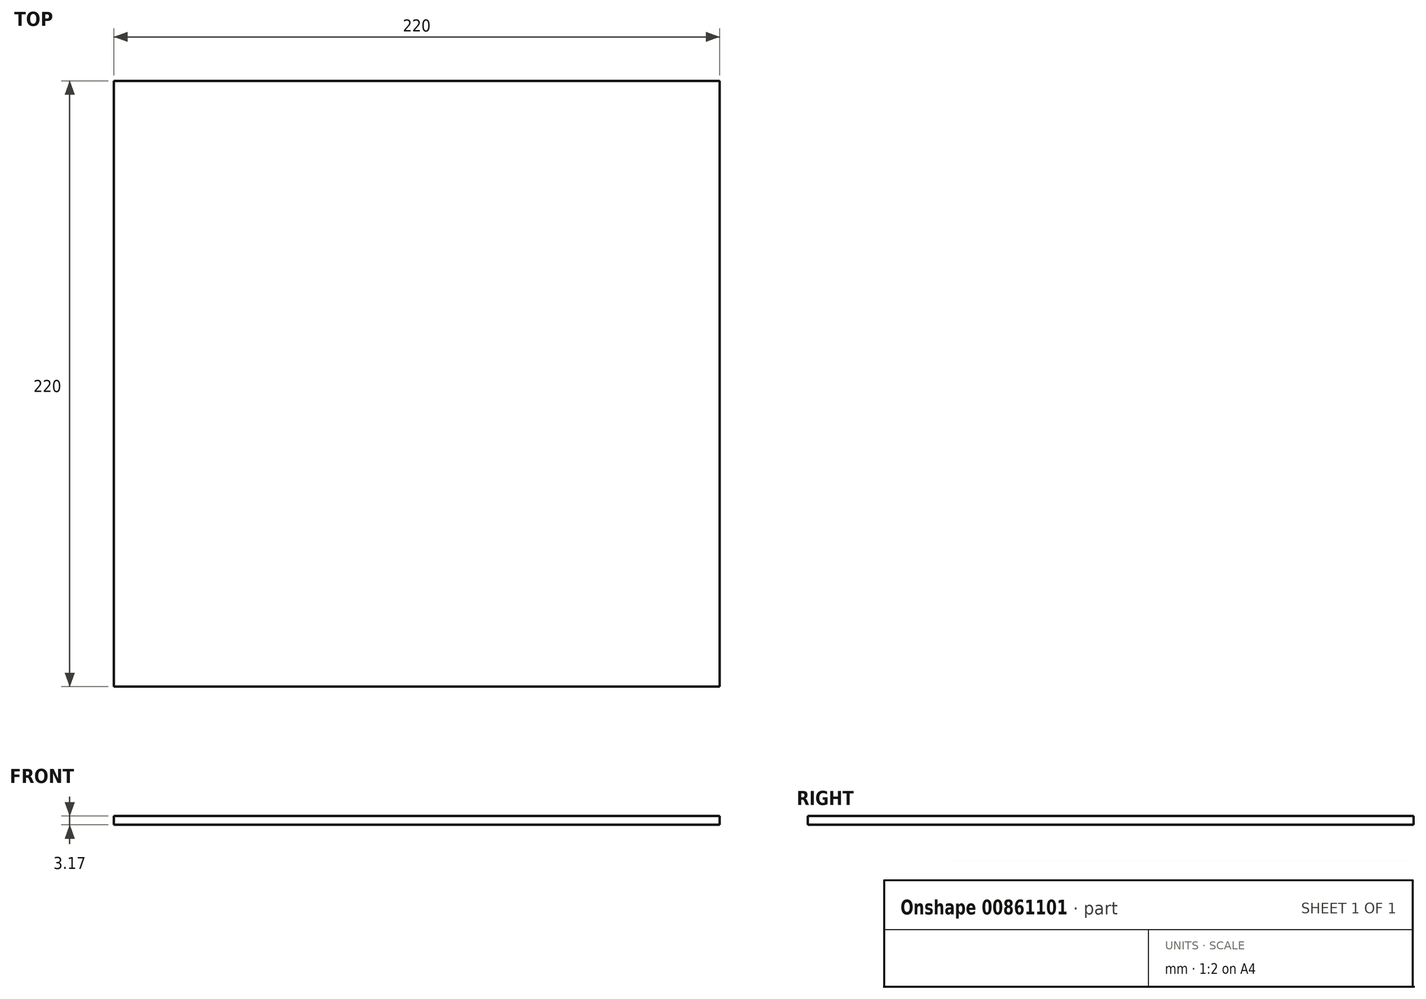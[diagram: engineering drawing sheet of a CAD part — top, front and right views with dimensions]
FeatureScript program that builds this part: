
annotation { "Feature Type Name" : "Feature", "Feature Type Description" : "" }
export const myFeature = defineFeature(function(context is Context, id is Id, definition is map)
    precondition{}
    {
        {
            var Q0;
            Q0=qCreatedBy(makeId("Top.planeOp"),FACE);
            var sketch = newSketch(context, id + "F0", { "sketchPlane" : qUnion([Q0])});
            skLineSegment(sketch, "E0.bottom", {"start": v(110, -110) * mm, "end": v(-110, -110) * mm});
            skLineSegment(sketch, "E0.top", {"start": v(110, 110) * mm, "end": v(-110, 110) * mm});
            skLineSegment(sketch, "E0.left", {"start": v(110, -110) * mm, "end": v(110, 110) * mm});
            skLineSegment(sketch, "E0.right", {"start": v(-110, -110) * mm, "end": v(-110, 110) * mm});
            skPoint(sketch, "E0.middle", {"position": v(0, 0) * mm});
            skSolve(sketch);
        }
        {
            var Q0;
            Q0 = qSketchRegion(id + "F0", true);
            extrude(context, id + "F1", {"entities" : qUnion([Q0]), "depth" : 3.17 * mm, "offsetDistance" : 25.4 * mm});
        }
    });
